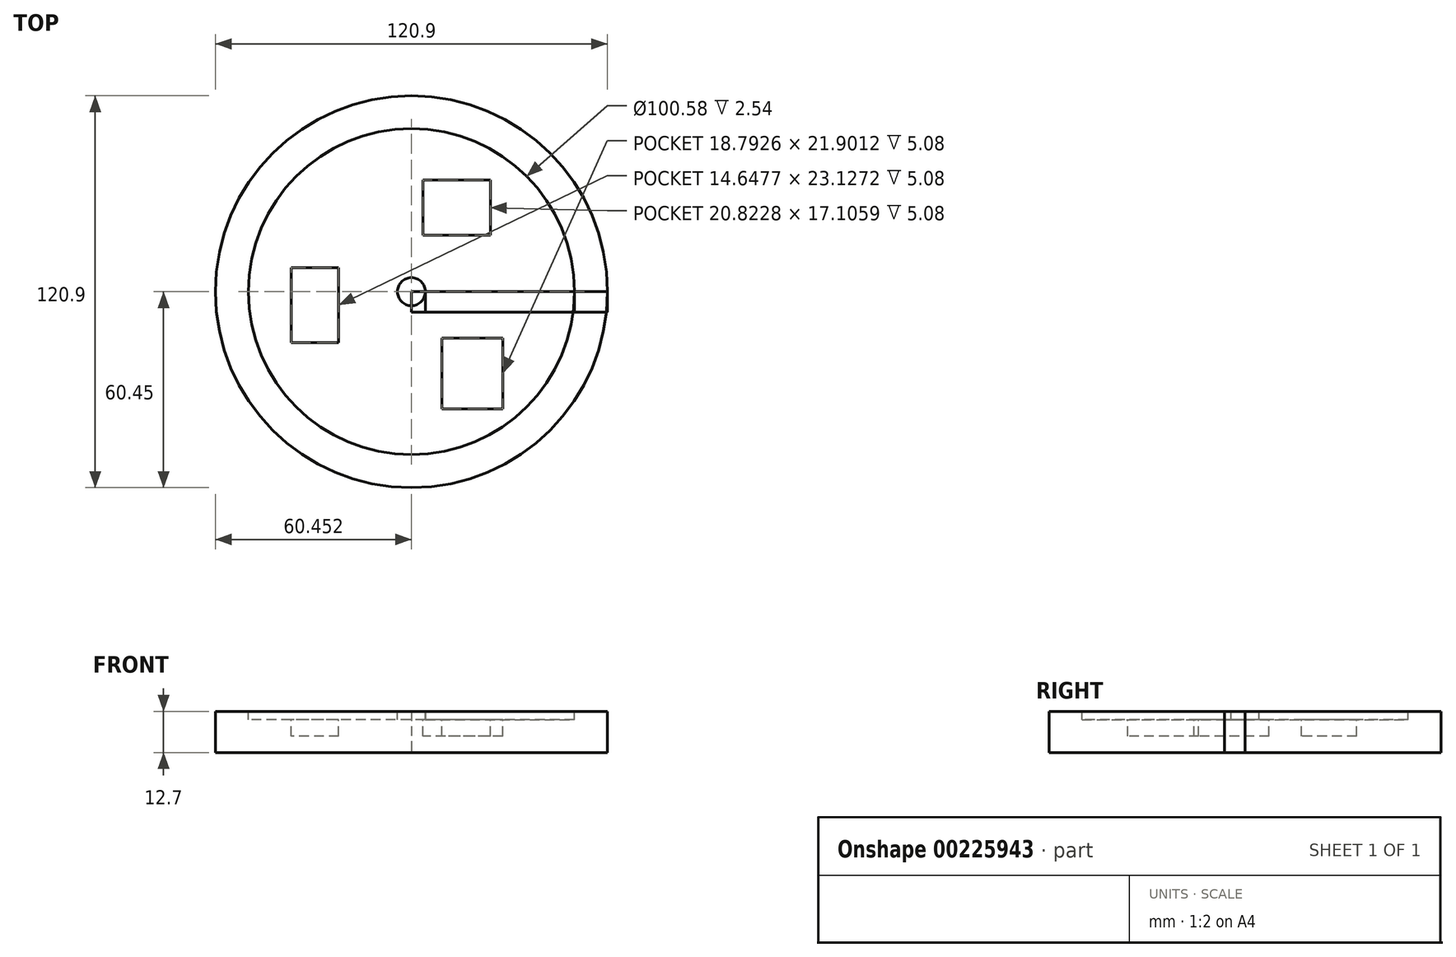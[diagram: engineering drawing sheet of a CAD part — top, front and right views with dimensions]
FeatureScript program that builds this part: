
annotation { "Feature Type Name" : "Feature", "Feature Type Description" : "" }
export const myFeature = defineFeature(function(context is Context, id is Id, definition is map)
    precondition{}
    {
        {
            var Q0;
            Q0=qCreatedBy(makeId("Front.planeOp"),FACE);
            var sketch = newSketch(context, id + "F0", { "sketchPlane" : qUnion([Q0])});
            skLineSegment(sketch, "E0", {"start": v(0, 0) * mm, "end": v(0, 12.7) * mm});
            skLineSegment(sketch, "E1", {"start": v(0, 12.7) * mm, "end": v(10.16, 12.7) * mm});
            skLineSegment(sketch, "E2", {"start": v(10.16, 12.7) * mm, "end": v(10.16, 10.16) * mm});
            skLineSegment(sketch, "E3", {"start": v(10.16, 10.16) * mm, "end": v(56.13, 10.16) * mm});
            skLineSegment(sketch, "E4", {"start": v(56.13, 10.16) * mm, "end": v(56.13, 12.7) * mm});
            skLineSegment(sketch, "E5", {"start": v(56.13, 12.7) * mm, "end": v(66.3, 12.7) * mm});
            skLineSegment(sketch, "E6", {"start": v(66.3, 12.7) * mm, "end": v(66.3, 0) * mm});
            skLineSegment(sketch, "E7", {"start": v(66.3, 0) * mm, "end": v(0, 0) * mm});
            skLineSegment(sketch, "E8", {"start": v(5.84, 15.24) * mm, "end": v(-0.5, 15.24) * mm});
            skLineSegment(sketch, "E9", {"start": v(-0.5, 15.24) * mm, "end": v(-10.88, 3.85) * mm});
            skLineSegment(sketch, "E10", {"start": v(0, 0) * mm, "end": v(-6.65, 0) * mm});
            skCircle(sketch, "E11", {"center": v(-6.65, 0) * mm, "radius": 5.72 * mm});
            skCircle(sketch, "E12", {"center": v(-6.65, 0) * mm, "radius": 3.18 * mm});
            skLineSegment(sketch, "E13", {"start": v(5.84, 15.24) * mm, "end": v(5.84, -9.4) * mm});
            skLineSegment(sketch, "E14", {"start": v(5.84, -9.4) * mm, "end": v(-8.18, -5.5) * mm});
            skSolve(sketch);
        }
        {
            var Q0;
            {var subQ0=sQuery(id+"F0.wireOp",EDGE,"E2");Q0=makeQuery(id+"F0.imprint","IMPRINT",FACE,{"disambiguationData":[TD([[makeQuery(id+"F0.imprint","IMPRINT",EDGE,{"derivedFrom":subQ0}),-1.0]])]});}
            var Q1;
            Q1=sQuery(id+"F0.wireOp",EDGE,"E13");
            revolve(context, id + "F1", {"entities" : qUnion([Q0]), "axis" : qUnion([Q1]), "revolveType" : RevolveType.FULL});
        }
        {
            var Q0;
            {var subQ0=sQuery(id+"F0.wireOp",EDGE,"E2");Q0=makeQuery(id+"F0.imprint","IMPRINT",FACE,{"disambiguationData":[TD([[makeQuery(id+"F0.imprint","IMPRINT",EDGE,{"derivedFrom":subQ0}),-1.0]])]});}
            extrude(context, id + "F2", {"entities" : qUnion([Q0]), "depth" : 6.35 * mm});
        }
        {
            var Q0;
            Q0=makeQuery(id+"F1.opRevolve","SWEPT_FACE",FACE,{"disambiguationData":[OSD([sQuery(id+"F0.wireOp",EDGE,"E3")])]});
            var sketch = newSketch(context, id + "F3", { "sketchPlane" : qUnion([Q0])});
            skLineSegment(sketch, "E15.bottom", {"start": v(30.17, 34.48) * mm, "end": v(9.35, 34.48) * mm});
            skLineSegment(sketch, "E15.top", {"start": v(30.17, 17.37) * mm, "end": v(9.35, 17.37) * mm});
            skLineSegment(sketch, "E15.left", {"start": v(30.17, 34.48) * mm, "end": v(30.17, 17.37) * mm});
            skLineSegment(sketch, "E15.right", {"start": v(9.35, 34.48) * mm, "end": v(9.35, 17.37) * mm});
            skLineSegment(sketch, "E16.bottom", {"start": v(34, -14.3) * mm, "end": v(15.21, -14.3) * mm});
            skLineSegment(sketch, "E16.top", {"start": v(34, -36.2) * mm, "end": v(15.21, -36.2) * mm});
            skLineSegment(sketch, "E16.left", {"start": v(34, -14.3) * mm, "end": v(34, -36.2) * mm});
            skLineSegment(sketch, "E16.right", {"start": v(15.21, -14.3) * mm, "end": v(15.21, -36.2) * mm});
            skLineSegment(sketch, "E17.bottom", {"start": v(-16.6, 7.44) * mm, "end": v(-31.24, 7.44) * mm});
            skLineSegment(sketch, "E17.top", {"start": v(-16.6, -15.68) * mm, "end": v(-31.24, -15.68) * mm});
            skLineSegment(sketch, "E17.left", {"start": v(-16.6, 7.44) * mm, "end": v(-16.6, -15.68) * mm});
            skLineSegment(sketch, "E17.right", {"start": v(-31.24, 7.44) * mm, "end": v(-31.24, -15.68) * mm});
            skSolve(sketch);
        }
        {
            var Q0;
            Q0=makeQuery(id+"F3.imprint","IMPRINT",FACE,{"disambiguationData":[TD([[makeQuery(id+"F3.imprint","IMPRINT",EDGE,{"derivedFrom":sQuery(id+"F3.wireOp",EDGE,"E16.bottom")}),1.0]])]});
            var Q1;
            Q1=makeQuery(id+"F3.imprint","IMPRINT",FACE,{"disambiguationData":[TD([[makeQuery(id+"F3.imprint","IMPRINT",EDGE,{"derivedFrom":sQuery(id+"F3.wireOp",EDGE,"E17.bottom")}),1.0]])]});
            var Q2;
            Q2=makeQuery(id+"F3.imprint","IMPRINT",FACE,{"disambiguationData":[TD([[makeQuery(id+"F3.imprint","IMPRINT",EDGE,{"derivedFrom":sQuery(id+"F3.wireOp",EDGE,"E15.bottom")}),1.0]])]});
            extrude(context, id + "F4", {"entities" : qUnion([Q0, Q1, Q2]), "operationType" : NewBodyOperationType.REMOVE, "oppositeDirection" : true, "depth" : 5.08 * mm});
        }
    });
